# Revit family: Construction_Other_Sjobergs_Drilling_Machine
name_source: partatom
category: Specialty Equipment
revit_build: Autodesk Revit 2017 (Build: 20190508_0315(x64)
units: mm (PartAtom-declared; Revit-internal decimal feet)

## family parameters
Always vertical = Yes
Cut with Voids When Loaded = No
OmniClass Number = 23.45.30.14.11
OmniClass Title = Commercial Dishwashers
Part Type = Normal
Room Calculation Point = No
Round Connector Dimension = Use Diameter
Shared = No
Work Plane-Based = No

## types (1)
- 37060 EJCA Drilling Machine S25T
    AssetType = Movable
    BIMObjectName = Construction_Other_Sjobergs_Drilling_Machine
    Brand = EJCA
    Category = Machines
    Color = Green
    Constituents = Accessories: Tool Package MK3 that includes: Machine vice 120 mm jaws; 2x T-groove nuts; Chuck 1–13 mm B '16 Metabo, Dorn; Reduction sleeve MK3 / MK2; Reduction sleeve MK3 / MK1
    ConvergoRefNr = 0184-2005-0022-SE
    Cost = 0 $
    DrillingMachineSizes = Drilling depth 135 mm. Table size 500x400 mm.
    DurationUnit = Year
    ElectricalDeviceNominalPower = 1500 W
    Features = CE-standard. Inclined gear in combination steel wheels against fiber wheels , low noise level and in it nearest maintenance-free gearbox. Drill head and table arm are rotatable 360 ° around the pillar, and can be raised and lowered.
    Finish = Cast iron
    HasProtectiveEarth = Yes
    IP_Code = IP 54
    IfcExportAs = IfcFurnishingElementType
    IfcExportType = TABLE
    MachineryMainMaterial = Grey metal
    MachineryQuaternaryMaterial = Clearance
    MachinerySecondaryMaterial = Black Metal
    MachineryTertiaryMaterial = Stainless Steel
    Manufacturer = Sjöbergs
    ManufacturerName = Sjöbergs
    ManufacturerURL = https://www.sjobergs.se
    Material = Metal, plastic
    Model = 37060 EJCA Drilling Machine S25T
    ModelReference = 37060
    Motor Power_230V50Hz = 0.55 kW / 0.75 kW
    Motor Power_230V60Hz = 0.55 kW / 0.75 kW
    Motor Power_3phase50Hz = 0.75 kW / 0.95 kW
    Motor Power_3phase60HZ = 0.75 kW / 0.95 kW
    NBSDescription = School art, design and technology tables and workbenches;
    NBSReference = 45-35-20/320
    Name = Sjobergs_Drilling_Machine
    NominalCurrent = 0 A
    NominalDepth = 650 mm
    NominalFrequencyRange = 0 Hz
    NominalHeight = 1710 mm
    NominalVoltage = 230 V
    NominalWidth = 500 mm
    NumberOfPoles = 0
    PhaseAngle = 0.00°
    ProductDatasheet = https://www.sjobergs.se
    Shape = Sculptured
    Size = 500x650x1710 mm
    SpindleSpeed_50Hz = 105-210-350-700-445-890-1460-2900
    SpindleSpeed_60Hz = 130-260-420-840-535-1070-1745-3480
    URL = https://www.sjobergs.se
    Uniclass2 = Pr_40_50_21
    Uniclass2015Description = Desks, Tables And Worktops
    Uniclass2015Reference = Pr_40_50_21_76
    UsageCurrent = 0 A
    Version = 1
    VersionDate = 01/07/2020
    WarrantyDurationUnit = Year
    Weight = 180.0 kg

## geometry (parser evidence)
native form markers: Extrusion x1, Sweep x4
no freeform markers — native parametric forms only
